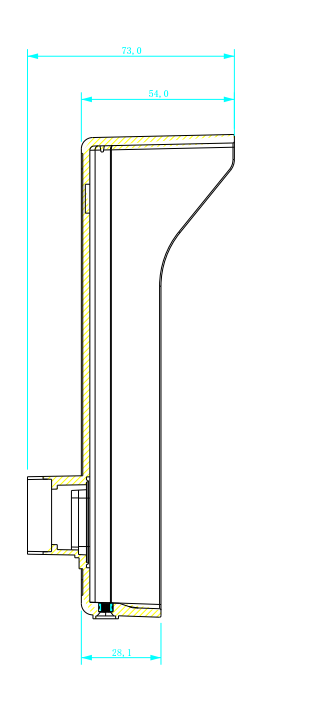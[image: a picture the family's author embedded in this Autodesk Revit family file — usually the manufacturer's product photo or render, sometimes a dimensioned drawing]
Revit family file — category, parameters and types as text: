
# Revit family: AV-03
name_source: partatom
category: Устройства связи
units: mm (PartAtom-declared; Revit-internal decimal feet)

## family parameters
Всегда вертикально = Нет
На основе рабочей плоскости = Да
Общий = Да
При загрузке вырезать с полостями = Нет
Размер круглого соединителя = Использовать диаметр
Сохранять ориентацию аннотаций = Нет
Тип детали = Нормальный
Точка принадлежности помещению = Нет

## types (1)
- AV-03
    ADSK_URL документации изделия = https://wiki.bas-ip.com
    ADSK_URL страницы изделия = https://www.bas-ip.ru
    ADSK_Версия Revit = Revit 2020
    ADSK_Единица измерения = шт
    ADSK_Завод-изготовитель = BAS-IP
    ADSK_Классификация нагрузок = Вызывная панель
    ADSK_Количество фаз = 1
    ADSK_Коэффициент мощности = 0.9
    ADSK_Марка = AV-03
    ADSK_Наименование = ВЫЗЫВНАЯ ПАНЕЛЬ AV-03
    ADSK_Наименование краткое = AV-03
    ADSK_Напряжение = 12 В
    ADSK_Номинальная мощность = 7 Вт
    ADSK_Полная мощность = 7 В·А
    ADSK_Размер_Длина = 160 мм
    ADSK_Размер_Толщина = 46 мм
    ADSK_Размер_Ширина = 102 мм
    BIM library = https://bimlib.ru
    URL = https://www.bas-ip.ru
    Аутентификация = Отдельный пароль на настройки, WEB–интерфейс
    Выходное видео = 720p (1280x720), H.264 Main Profile
    Группа модели = Вызывная панель
    Дисплей = Нет
    Дополнительно = SIP P2P, Встроенное реле
    Изготовитель = BAS-IP
    Изображение типоразмера = <Нет>
    Интеграция со СКУД = Выход WIEGAND-26, 32, 34, 37, 40, 42, 56, 58, 64 бит
    Интерфейс = Мультиязычный WEB–интерфейс
    Камера = 1/4”
    Класс степени защиты = IP64
    Кнопки быстрого вызова = 1 сенсорная кнопка вызова
    Количество мелодий подтверждения вызова = 1 полифоническая мелодия
    Контроль доступа AV-03BD GREY = Мультиформатный считыватель с поддержкой технологии UKEY
    Контроль доступа AV-03D GREY = Нет
    Контроль доступа AV-03ED GREY = Считыватель Em-Marin
    Контроль доступа AV-03MD GREY = Считыватель Mifare
    Корпус = ABS пластик
    Материал корпуса = Материал серый
    Минимальная освещенность = 0,01 LuX
    Ночная подсветка = 6 светодиодов
    Описание = BAS-IP AV-03 - это стильная панель, которая, несомненно, идеально впишется в интерьер любого офисного центра. Панель изготовлена из высококачественного пластика и может использоваться практически в любом помещении
    Открытие замка = С монитора, из приложения BAS-IP Intercom, по карте, из приложения UKEY
    Отметка по умолчанию = 0 мм
    Питание = + 12 Вольт, PoE
    Поддерживаемые аудиокодеки = G.711u
    Потребление питания = 6,5 Вт, в режиме ожидания – 2,5 Вт
    Размер под установку = 25х60х40 мм
    Размер самой панели = 102х160х46 мм
    Разрешение камеры = 1.0 Мп
    Режим разговора = Двухсторонний
    Температурный режим = -40 ... +65 °С
    Тип панели = Индивидуальная
    Тип установки = Накладная
    Угол обзора = По горизонтали 110°, по вертикали 60°
    Цветовое решение = Серебо, Черный
